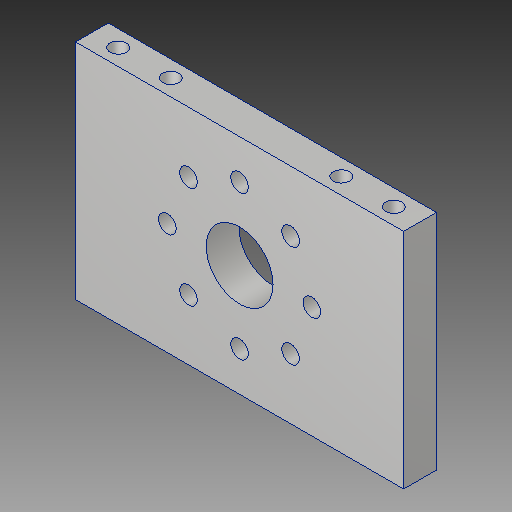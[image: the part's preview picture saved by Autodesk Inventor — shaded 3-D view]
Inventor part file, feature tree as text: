
AUTODESK INVENTOR PART (.ipt)
format: ipt  version: 2019 (Build 230136000, 136)  size: 164,864 bytes
history: native  units: mm
features: extrude x3, sketch x3, other x1, projected_geometry x1
ambient origin geometry x8: Origin, YZ Plane, XZ Plane, XY Plane, X Axis, Y Axis, Z Axis, Center Point
bodies: Body1 (feature_tree)
feature tree (8):
  other  "솔리드1"
  extrude  "돌출1"  Depth=50.0mm
  extrude  "돌출2"  Depth=34.0mm
  extrude  "돌출3"  Depth=17.0mm
  sketch  "스케치1"
  sketch  "스케치2"
  sketch  "스케치3"
  projected_geometry  "투영된 루프1"
